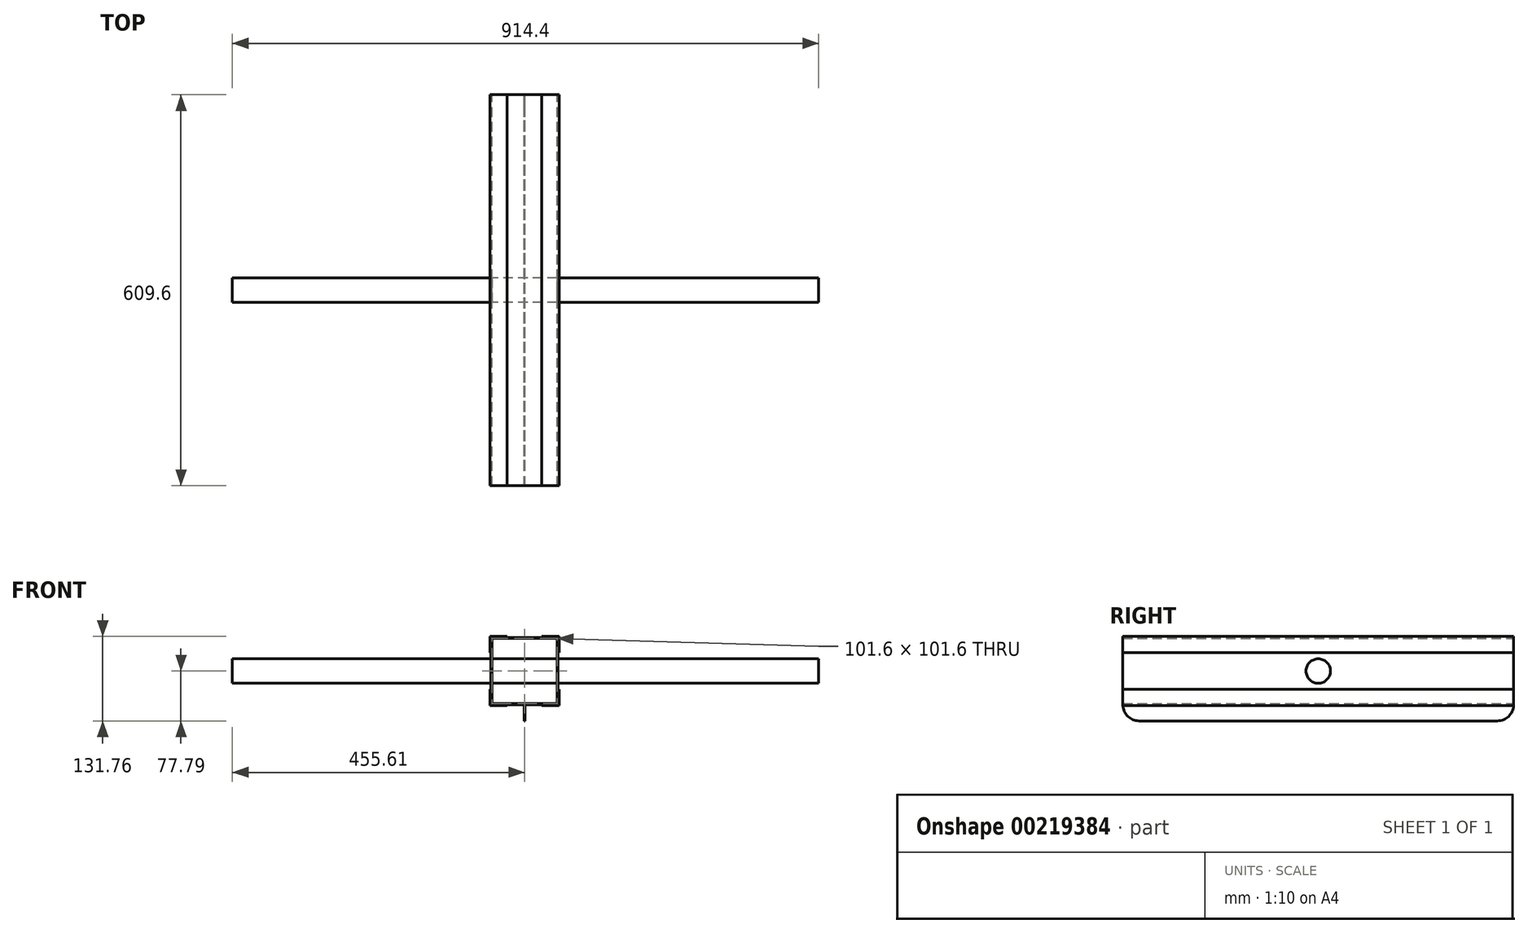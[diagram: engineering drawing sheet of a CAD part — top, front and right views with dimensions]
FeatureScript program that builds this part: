
annotation { "Feature Type Name" : "Feature", "Feature Type Description" : "" }
export const myFeature = defineFeature(function(context is Context, id is Id, definition is map)
    precondition{}
    {
        {
            var Q0;
            Q0=qCreatedBy(makeId("Front.planeOp"),FACE);
            var sketch = newSketch(context, id + "F0", { "sketchPlane" : qUnion([Q0])});
            skLineSegment(sketch, "E0.bottom", {"start": v(-101.6, 0) * mm, "end": v(0, 0) * mm});
            skLineSegment(sketch, "E0.top", {"start": v(-101.6, -101.6) * mm, "end": v(0, -101.6) * mm});
            skLineSegment(sketch, "E0.left", {"start": v(-101.6, 0) * mm, "end": v(-101.6, -101.6) * mm});
            skLineSegment(sketch, "E0.right", {"start": v(0, 0) * mm, "end": v(0, -101.6) * mm});
            skLineSegment(sketch, "E1.0", {"start": v(-103.19, 1.59) * mm, "end": v(1.59, 1.59) * mm});
            skLineSegment(sketch, "E1.1", {"start": v(-103.19, 1.59) * mm, "end": v(-103.19, -103.19) * mm});
            skLineSegment(sketch, "E1.2", {"start": v(-103.19, -103.19) * mm, "end": v(1.59, -103.19) * mm});
            skLineSegment(sketch, "E1.3", {"start": v(1.59, 1.59) * mm, "end": v(1.59, -103.19) * mm});
            skLineSegment(sketch, "E2", {"start": v(0, 0) * mm, "end": v(-101.6, -101.6) * mm, "construction": true});
            skLineSegment(sketch, "E3", {"start": v(-77.79, 1.59) * mm, "end": v(-77.79, 3.17) * mm});
            skLineSegment(sketch, "E4", {"start": v(-77.79, 3.17) * mm, "end": v(-104.78, 3.17) * mm});
            skLineSegment(sketch, "E5", {"start": v(-104.78, 3.17) * mm, "end": v(-104.78, -22.23) * mm});
            skLineSegment(sketch, "E6", {"start": v(-104.78, -22.23) * mm, "end": v(-103.19, -22.23) * mm});
            skLineSegment(sketch, "E7", {"start": v(-50.8, 0) * mm, "end": v(-50.8, -101.6) * mm, "construction": true});
            skLineSegment(sketch, "E8.MirrorCS", {"start": v(3.17, 3.18) * mm, "end": v(3.18, -22.22) * mm});
            skLineSegment(sketch, "E9.MirrorCS", {"start": v(-23.81, 3.18) * mm, "end": v(3.17, 3.18) * mm});
            skLineSegment(sketch, "E10.MirrorCS", {"start": v(-23.81, 1.59) * mm, "end": v(-23.81, 3.18) * mm});
            skLineSegment(sketch, "E11.MirrorCS", {"start": v(3.17, -22.22) * mm, "end": v(1.59, -22.22) * mm});
            skLineSegment(sketch, "E12", {"start": v(0, -50.8) * mm, "end": v(-101.6, -50.8) * mm, "construction": true});
            skLineSegment(sketch, "E13.MirrorCS", {"start": v(-104.78, -104.78) * mm, "end": v(-104.78, -79.38) * mm});
            skLineSegment(sketch, "E14.MirrorCS", {"start": v(-77.79, -104.78) * mm, "end": v(-104.78, -104.78) * mm});
            skLineSegment(sketch, "E15.MirrorCS", {"start": v(-77.79, -103.19) * mm, "end": v(-77.79, -104.78) * mm});
            skLineSegment(sketch, "E16.MirrorCS", {"start": v(-104.77, -79.38) * mm, "end": v(-103.19, -79.38) * mm});
            skLineSegment(sketch, "E17.MirrorCS", {"start": v(3.18, -104.78) * mm, "end": v(3.18, -79.38) * mm});
            skLineSegment(sketch, "E18.MirrorCS", {"start": v(-23.81, -104.78) * mm, "end": v(3.18, -104.78) * mm});
            skLineSegment(sketch, "E19.MirrorCS", {"start": v(3.18, -79.38) * mm, "end": v(1.59, -79.38) * mm});
            skLineSegment(sketch, "E20.MirrorCS", {"start": v(-23.81, -103.19) * mm, "end": v(-23.81, -104.78) * mm});
            skSolve(sketch);
        }
        {
            var Q0;
            {var subQ0=sQuery(id+"F0.wireOp",EDGE,"E3");Q0=makeQuery(id+"F0.imprint","IMPRINT",FACE,{"disambiguationData":[TD([[makeQuery(id+"F0.imprint","IMPRINT",EDGE,{"derivedFrom":subQ0}),1.0]])]});}
            var Q1;
            Q1=makeQuery(id+"F0.imprint","IMPRINT",FACE,{"disambiguationData":[TD([[makeQuery(id+"F0.imprint","IMPRINT",EDGE,{"derivedFrom":sQuery(id+"F0.wireOp",EDGE,"E0.bottom")}),1.0]])]});
            var Q2;
            Q2=makeQuery(id+"F0.imprint","IMPRINT",FACE,{"disambiguationData":[TD([[makeQuery(id+"F0.imprint","IMPRINT",EDGE,{"derivedFrom":sQuery(id+"F0.wireOp",EDGE,"E14.MirrorCS")}),-1.0]])]});
            var Q3;
            Q3=makeQuery(id+"F0.imprint","IMPRINT",FACE,{"disambiguationData":[TD([[makeQuery(id+"F0.imprint","IMPRINT",EDGE,{"derivedFrom":sQuery(id+"F0.wireOp",EDGE,"E17.MirrorCS")}),1.0]])]});
            var Q4;
            Q4=makeQuery(id+"F0.imprint","IMPRINT",FACE,{"disambiguationData":[TD([[makeQuery(id+"F0.imprint","IMPRINT",EDGE,{"derivedFrom":sQuery(id+"F0.wireOp",EDGE,"E8.MirrorCS")}),-1.0]])]});
            extrude(context, id + "F1", {"entities" : qUnion([Q0, Q1, Q2, Q3, Q4]), "depth" : 609.6 * mm});
        }
        {
            var Q0;
            Q0=makeQuery(id+"F1.opExtrude","SWEPT_FACE",FACE,{"disambiguationData":[OSD([sQuery(id+"F0.wireOp",EDGE,"E1.3")])]});
            var sketch = newSketch(context, id + "F2", { "sketchPlane" : qUnion([Q0])});
            skLineSegment(sketch, "E21", {"start": v(-609.6, -50.8) * mm, "end": v(0, -50.8) * mm, "construction": true});
            skCircle(sketch, "E22", {"center": v(-304.8, -50.8) * mm, "radius": 19.05 * mm});
            skSolve(sketch);
        }
        {
            var Q0;
            Q0=makeQuery(id+"F2.imprint","IMPRINT",FACE,{"disambiguationData":[TD([[makeQuery(id+"F2.imprint","IMPRINT",EDGE,{"derivedFrom":sQuery(id+"F2.wireOp",EDGE,"E22")}),1.0]])]});
            extrude(context, id + "F3", {"entities" : qUnion([Q0]), "operationType" : NewBodyOperationType.ADD, "depth" : 406.4 * mm, "hasSecondDirection" : true, "secondDirectionOppositeDirection" : true, "secondDirectionDepth" : 508 * mm});
        }
        {
            var Q0;
            Q0=makeQuery(id+"F1.opExtrude","SWEPT_FACE",FACE,{"disambiguationData":[OSD([sQuery(id+"F0.wireOp",EDGE,"E1.2")])]});
            var sketch = newSketch(context, id + "F4", { "sketchPlane" : qUnion([Q0])});
            skLineSegment(sketch, "E23", {"start": v(-50.8, 609.6) * mm, "end": v(-50.8, 0) * mm});
            skLineSegment(sketch, "E24", {"start": v(-50, 609.6) * mm, "end": v(-50, 0) * mm});
            skLineSegment(sketch, "E25.MirrorCS", {"start": v(-51.6, 609.6) * mm, "end": v(-51.6, 0) * mm});
            skSolve(sketch);
        }
        {
            var Q0;
            {var subQ0=sQuery(id+"F4.wireOp",EDGE,"E23");Q0=makeQuery(id+"F4.imprint","IMPRINT",FACE,{"disambiguationData":[TD([[makeQuery(id+"F4.imprint","IMPRINT",EDGE,{"derivedFrom":subQ0}),1.0]])]});}
            var Q1;
            {var subQ0=sQuery(id+"F4.wireOp",EDGE,"E23");Q1=makeQuery(id+"F4.imprint","IMPRINT",FACE,{"disambiguationData":[TD([[makeQuery(id+"F4.imprint","IMPRINT",EDGE,{"derivedFrom":subQ0}),-1.0]])]});}
            extrude(context, id + "F5", {"entities" : qUnion([Q0, Q1]), "operationType" : NewBodyOperationType.ADD, "depth" : 25.4 * mm});
        }
        {
            var Q0;
            {var subQ0=sQuery(id+"F0.wireOp",EDGE,"E1.2");var subQ1=makeQuery(id+"F1.opExtrude","CAP_EDGE",EDGE,{"disambiguationData":[OSD([subQ0])],"isStart":true});var subQ2=makeQuery(id+"F4.imprint","INTERSECT",VERTEX,{"derivedFrom":[subQ1,sQuery(id+"F4.wireOp",EDGE,"E23")]});Q0=makeQuery(id+"F5.opExtrude","CAP_EDGE",EDGE,{"disambiguationData":[OSD([subQ0]),TDD([makeQuery(id+"F4.imprint","IMPRINT",EDGE,{"disambiguationData":[TD([[subQ2,-1.0]])],"derivedFrom":subQ1}),makeQuery(id+"F4.imprint","IMPRINT",EDGE,{"disambiguationData":[TD([[subQ2,1.0]])],"derivedFrom":subQ1})])],"isStart":false});}
            fillet(context, id + "F6", {"entities" : qUnion([Q0]), "radius" : 25.4 * mm, "tangentPropagation" : true, "allowEdgeOverflow" : false});
        }
        {
            var Q0;
            {var subQ0=sQuery(id+"F0.wireOp",EDGE,"E1.2");var subQ1=makeQuery(id+"F1.opExtrude","CAP_EDGE",EDGE,{"disambiguationData":[OSD([subQ0])],"isStart":false});var subQ2=makeQuery(id+"F4.imprint","INTERSECT",VERTEX,{"derivedFrom":[subQ1,sQuery(id+"F4.wireOp",EDGE,"E23")]});Q0=makeQuery(id+"F5.opExtrude","CAP_EDGE",EDGE,{"disambiguationData":[OSD([subQ0]),TDD([makeQuery(id+"F4.imprint","IMPRINT",EDGE,{"disambiguationData":[TD([[subQ2,-1.0]])],"derivedFrom":subQ1}),makeQuery(id+"F4.imprint","IMPRINT",EDGE,{"disambiguationData":[TD([[subQ2,1.0]])],"derivedFrom":subQ1})])],"isStart":false});}
            fillet(context, id + "F7", {"entities" : qUnion([Q0]), "radius" : 25.4 * mm, "tangentPropagation" : true, "allowEdgeOverflow" : false});
        }
    });
